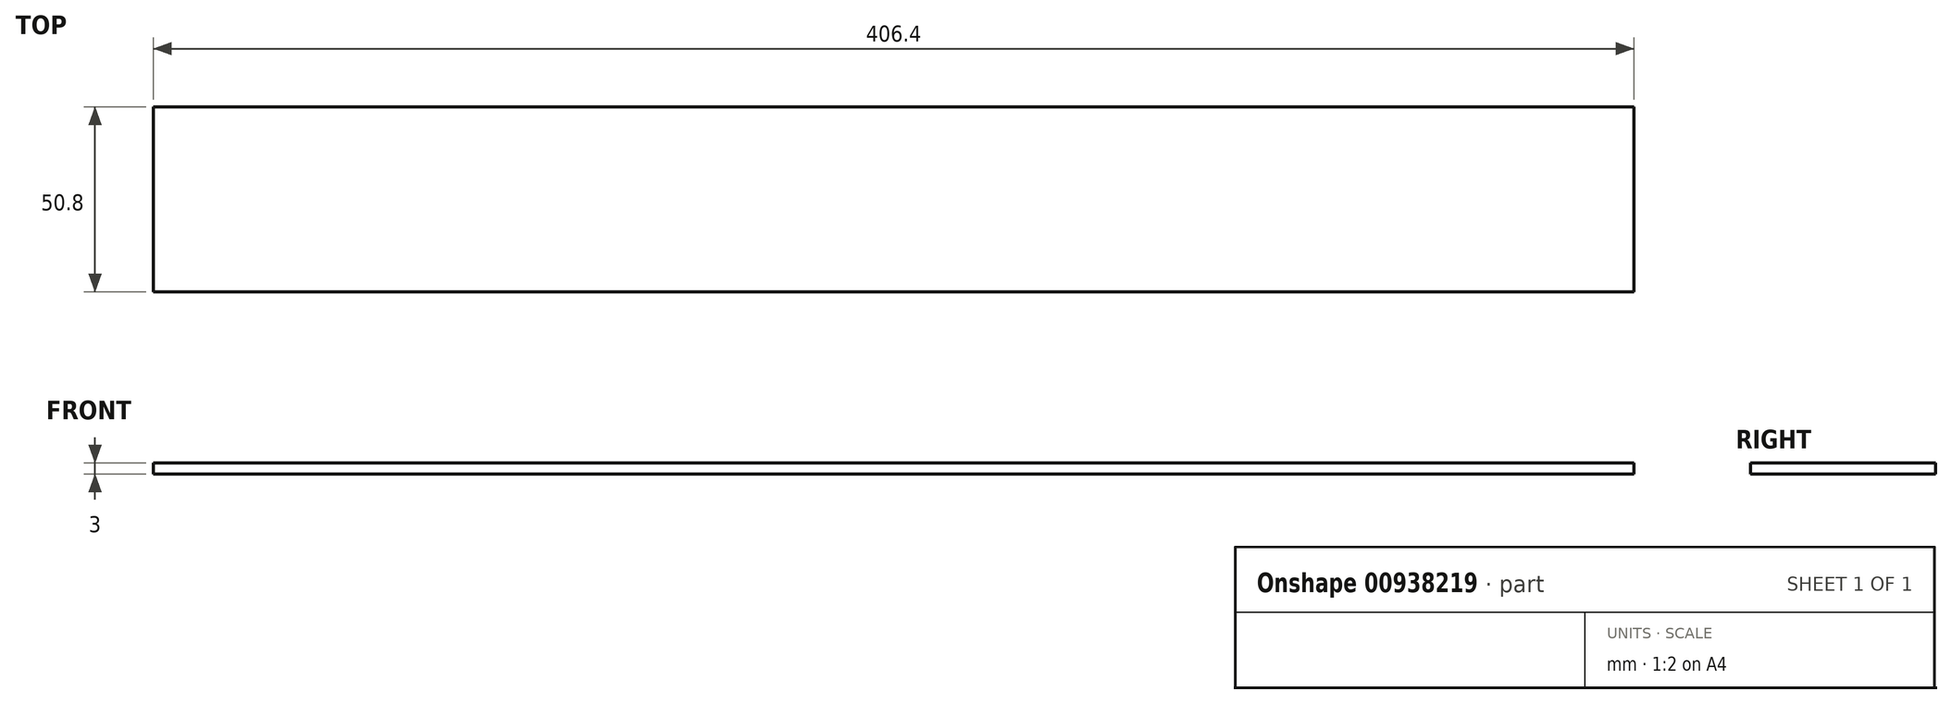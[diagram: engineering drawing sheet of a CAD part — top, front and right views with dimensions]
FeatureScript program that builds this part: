
annotation { "Feature Type Name" : "Feature", "Feature Type Description" : "" }
export const myFeature = defineFeature(function(context is Context, id is Id, definition is map)
    precondition{}
    {
        {
            var Q0;
            Q0=qCreatedBy(makeId("Top.planeOp"),FACE);
            var sketch = newSketch(context, id + "F0", { "sketchPlane" : qUnion([Q0])});
            skLineSegment(sketch, "E0.bottom", {"start": v(0, 0) * mm, "end": v(406.4, 0) * mm});
            skLineSegment(sketch, "E0.top", {"start": v(0, 50.8) * mm, "end": v(406.4, 50.8) * mm});
            skLineSegment(sketch, "E0.left", {"start": v(0, 0) * mm, "end": v(0, 50.8) * mm});
            skLineSegment(sketch, "E0.right", {"start": v(406.4, 0) * mm, "end": v(406.4, 50.8) * mm});
            skSolve(sketch);
        }
        {
            var Q0;
            Q0=makeQuery(id+"F0.imprint","IMPRINT",FACE,{"disambiguationData":[TD([[makeQuery(id+"F0.imprint","IMPRINT",EDGE,{"derivedFrom":sQuery(id+"F0.wireOp",EDGE,"E0.bottom")}),1.0]])]});
            extrude(context, id + "F1", {"entities" : qUnion([Q0]), "depth" : 3 * mm, "offsetDistance" : 25 * mm});
        }
    });
